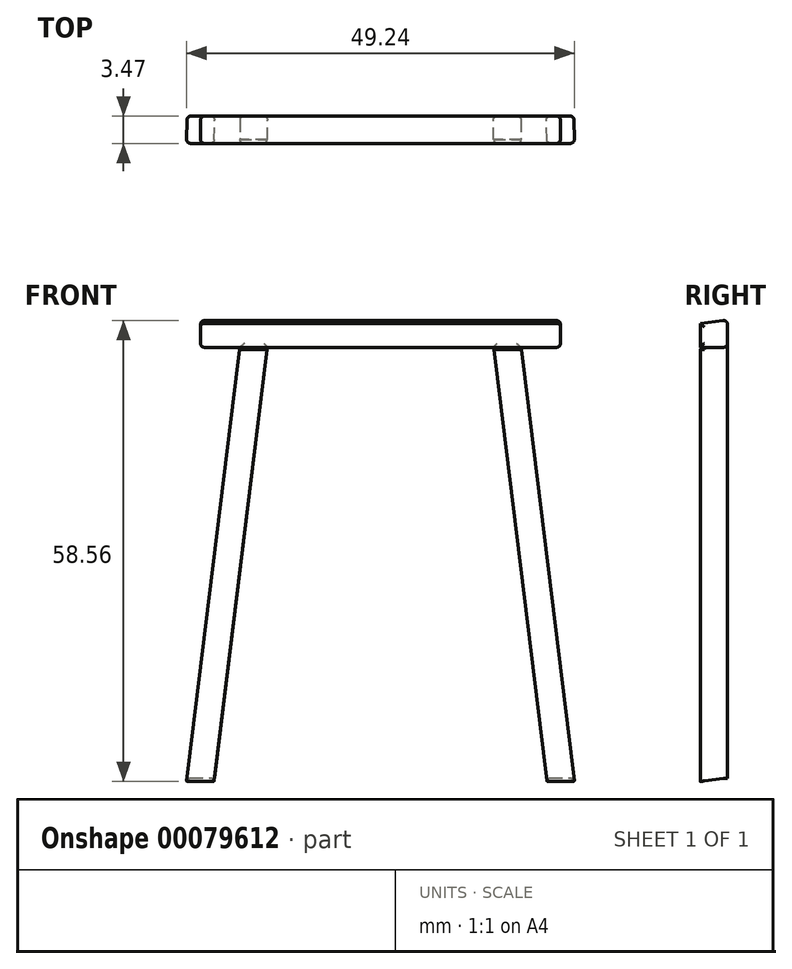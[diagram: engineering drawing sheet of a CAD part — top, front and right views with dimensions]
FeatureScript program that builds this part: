
annotation { "Feature Type Name" : "Feature", "Feature Type Description" : "" }
export const myFeature = defineFeature(function(context is Context, id is Id, definition is map)
    precondition{}
    {
        {
            var Q0;
            Q0=qCreatedBy(makeId("Front.planeOp"),FACE);
            var sketch = newSketch(context, id + "F0", { "sketchPlane" : qUnion([Q0])});
            skLineSegment(sketch, "E0.bottom", {"start": v(-22.86, -2.57) * mm, "end": v(22.86, -2.57) * mm});
            skLineSegment(sketch, "E0.top", {"start": v(-22.86, -6.05) * mm, "end": v(22.86, -6.05) * mm});
            skLineSegment(sketch, "E0.left", {"start": v(-22.86, -2.57) * mm, "end": v(-22.86, -6.05) * mm});
            skLineSegment(sketch, "E0.right", {"start": v(22.86, -2.57) * mm, "end": v(22.86, -6.05) * mm});
            skSolve(sketch);
        }
        {
            var Q0;
            Q0 = qSketchRegion(id + "F0", true);
            extrude(context, id + "F1", {"entities" : qUnion([Q0]), "depth" : 3.47 * mm});
        }
        {
            var Q0;
            Q0=makeQuery(id+"F1.opExtrude","CAP_FACE",FACE,{"disambiguationData":[OSD([sQuery(id+"F0.wireOp",EDGE,"E0.bottom"),sQuery(id+"F0.wireOp",EDGE,"E0.top"),sQuery(id+"F0.wireOp",EDGE,"E0.left"),sQuery(id+"F0.wireOp",EDGE,"E0.right")])],"isStart":false});
            var sketch = newSketch(context, id + "F2", { "sketchPlane" : qUnion([Q0])});
            skLineSegment(sketch, "E1", {"start": v(-17.43, -2.57) * mm, "end": v(-24.63, -61.2) * mm});
            skLineSegment(sketch, "E2", {"start": v(-24.63, -61.2) * mm, "end": v(-21.18, -61.63) * mm});
            skLineSegment(sketch, "E3", {"start": v(-21.18, -61.63) * mm, "end": v(-13.93, -2.57) * mm});
            skLineSegment(sketch, "E4", {"start": v(-13.93, -2.57) * mm, "end": v(-17.43, -2.57) * mm});
            skLineSegment(sketch, "E5.MirrorCS", {"start": v(24.63, -61.2) * mm, "end": v(21.18, -61.63) * mm});
            skLineSegment(sketch, "E6.MirrorCS", {"start": v(13.93, -2.57) * mm, "end": v(17.43, -2.57) * mm});
            skLineSegment(sketch, "E7.MirrorCS", {"start": v(17.43, -2.57) * mm, "end": v(24.63, -61.2) * mm});
            skLineSegment(sketch, "E8.MirrorCS", {"start": v(21.18, -61.63) * mm, "end": v(13.93, -2.57) * mm});
            skSolve(sketch);
        }
        {
            var Q0;
            Q0 = qSketchRegion(id + "F2", true);
            extrude(context, id + "F3", {"entities" : qUnion([Q0]), "operationType" : NewBodyOperationType.ADD, "oppositeDirection" : true, "depth" : 3.47 * mm});
        }
        {
            var Q0;
            Q0=qCreatedBy(makeId("Right.planeOp"),FACE);
            var sketch = newSketch(context, id + "F4", { "sketchPlane" : qUnion([Q0])});
            skLineSegment(sketch, "E9", {"start": v(0, -2.57) * mm, "end": v(-3.47, -2.57) * mm});
            skLineSegment(sketch, "E10", {"start": v(0, -2.57) * mm, "end": v(-3.47, -3) * mm});
            skLineSegment(sketch, "E11", {"start": v(-3.47, -2.57) * mm, "end": v(-3.47, -3) * mm});
            skPoint(sketch, "E12.orphan", {"position": v(-3.47, -3.03) * mm});
            skPoint(sketch, "E13.orphan", {"position": v(-3.7, -3.03) * mm});
            skLineSegment(sketch, "E14", {"start": v(-3.47, -61.2) * mm, "end": v(0, -60.78) * mm});
            skLineSegment(sketch, "E15", {"start": v(0, -60.78) * mm, "end": v(0, -61.96) * mm});
            skLineSegment(sketch, "E16", {"start": v(0, -61.96) * mm, "end": v(-3.47, -61.96) * mm});
            skLineSegment(sketch, "E17", {"start": v(-3.47, -61.96) * mm, "end": v(-3.47, -61.2) * mm});
            skSolve(sketch);
        }
        {
            var Q0;
            Q0 = qSketchRegion(id + "F4", true);
            extrude(context, id + "F5", {"entities" : qUnion([Q0]), "operationType" : NewBodyOperationType.REMOVE, "oppositeDirection" : true, "depth" : 76.2 * mm, "symmetric" : true});
        }
        {
            var Q0;
            Q0=makeQuery(id+"F3.boolean.opBoolean","MERGE",FACE,{"derivedFrom":[makeQuery(id+"F1.opExtrude","CAP_FACE",FACE,{"disambiguationData":[OSD([sQuery(id+"F0.wireOp",EDGE,"E0.bottom"),sQuery(id+"F0.wireOp",EDGE,"E0.top"),sQuery(id+"F0.wireOp",EDGE,"E0.left"),sQuery(id+"F0.wireOp",EDGE,"E0.right")])],"isStart":false}),makeQuery(id+"F3.opExtrude","CAP_FACE",FACE,{"disambiguationData":[OSD([sQuery(id+"F2.wireOp",EDGE,"E1"),sQuery(id+"F2.wireOp",EDGE,"E2"),sQuery(id+"F2.wireOp",EDGE,"E3"),sQuery(id+"F2.wireOp",EDGE,"E4")])],"isStart":true}),makeQuery(id+"F3.opExtrude","CAP_FACE",FACE,{"disambiguationData":[OSD([sQuery(id+"F2.wireOp",EDGE,"E5.MirrorCS"),sQuery(id+"F2.wireOp",EDGE,"E6.MirrorCS"),sQuery(id+"F2.wireOp",EDGE,"E7.MirrorCS"),sQuery(id+"F2.wireOp",EDGE,"E8.MirrorCS")])],"isStart":true})]});
            var sketch = newSketch(context, id + "F6", { "sketchPlane" : qUnion([Q0])});
            skLineSegment(sketch, "E18", {"start": v(-22.86, -6.05) * mm, "end": v(22.86, -6.05) * mm});
            skLineSegment(sketch, "E19", {"start": v(22.86, -6.05) * mm, "end": v(22.86, -6.3) * mm});
            skLineSegment(sketch, "E20", {"start": v(22.86, -6.3) * mm, "end": v(-22.86, -6.3) * mm});
            skLineSegment(sketch, "E21", {"start": v(-22.86, -6.3) * mm, "end": v(-22.86, -6.05) * mm});
            skSolve(sketch);
        }
        {
            var Q0;
            Q0 = qSketchRegion(id + "F6", true);
            extrude(context, id + "F7", {"entities" : qUnion([Q0]), "operationType" : NewBodyOperationType.REMOVE, "oppositeDirection" : true, "depth" : 0.5 * mm});
        }
        {
            var Q0;
            Q0=makeQuery(id+"F5.boolean.opBoolean","COPY",EDGE,{"derivedFrom":makeQuery(id+"F5.opExtrude","SWEPT_EDGE",EDGE,{"disambiguationData":[OSD([sQuery(id+"F4.wireOp",EDGE,"E10"),sQuery(id+"F4.wireOp",EDGE,"E11")])]})});
            var Q1;
            Q1=makeQuery(id+"F1.opExtrude","SWEPT_FACE",FACE,{"disambiguationData":[OSD([sQuery(id+"F0.wireOp",EDGE,"E0.right")])]});
            var Q2;
            Q2=makeQuery(id+"F3.opExtrude","CAP_EDGE",EDGE,{"disambiguationData":[OSD([sQuery(id+"F2.wireOp",EDGE,"E7.MirrorCS")])],"isStart":true});
            var Q3;
            Q3=makeQuery(id+"F3.opExtrude","CAP_EDGE",EDGE,{"disambiguationData":[OSD([sQuery(id+"F2.wireOp",EDGE,"E3")])],"isStart":true});
            var Q4;
            Q4=makeQuery(id+"F3.opExtrude","CAP_EDGE",EDGE,{"disambiguationData":[OSD([sQuery(id+"F2.wireOp",EDGE,"E1")])],"isStart":true});
            var Q5;
            Q5=makeQuery(id+"F1.opExtrude","SWEPT_FACE",FACE,{"disambiguationData":[OSD([sQuery(id+"F0.wireOp",EDGE,"E0.left")])]});
            var Q6;
            Q6=makeQuery(id+"F3.opExtrude","CAP_EDGE",EDGE,{"disambiguationData":[OSD([sQuery(id+"F2.wireOp",EDGE,"E8.MirrorCS")])],"isStart":true});
            var Q7;
            {var subQ0=sQuery(id+"F0.wireOp",EDGE,"E0.right");var subQ1=sQuery(id+"F0.wireOp",EDGE,"E0.top");Q7=makeQuery(id+"F3.boolean.opBoolean","SPLIT",EDGE,{"disambiguationData":[TD([makeQuery(id+"F1.opExtrude","SWEPT_FACE",FACE,{"disambiguationData":[OSD([subQ0])]})])],"derivedFrom":makeQuery(id+"F1.opExtrude","CAP_EDGE",EDGE,{"disambiguationData":[OSD([subQ1])],"isStart":true})});}
            var Q8;
            Q8=makeQuery(id+"F3.opExtrude","CAP_EDGE",EDGE,{"disambiguationData":[OSD([sQuery(id+"F2.wireOp",EDGE,"E8.MirrorCS")])],"isStart":false});
            var Q9;
            {var subQ0=sQuery(id+"F2.wireOp",EDGE,"E3");var subQ1=sQuery(id+"F0.wireOp",EDGE,"E0.top");Q9=makeQuery(id+"F3.boolean.opBoolean","SPLIT",EDGE,{"disambiguationData":[TD([makeQuery(id+"F3.opExtrude","SWEPT_FACE",FACE,{"disambiguationData":[OSD([subQ0])]})])],"derivedFrom":makeQuery(id+"F1.opExtrude","CAP_EDGE",EDGE,{"disambiguationData":[OSD([subQ1])],"isStart":true})});}
            var Q10;
            {var subQ0=sQuery(id+"F0.wireOp",EDGE,"E0.left");var subQ1=sQuery(id+"F0.wireOp",EDGE,"E0.top");Q10=makeQuery(id+"F3.boolean.opBoolean","SPLIT",EDGE,{"disambiguationData":[TD([makeQuery(id+"F1.opExtrude","SWEPT_FACE",FACE,{"disambiguationData":[OSD([subQ0])]})])],"derivedFrom":makeQuery(id+"F1.opExtrude","CAP_EDGE",EDGE,{"disambiguationData":[OSD([subQ1])],"isStart":true})});}
            var Q11;
            Q11=makeQuery(id+"F3.opExtrude","CAP_EDGE",EDGE,{"disambiguationData":[OSD([sQuery(id+"F2.wireOp",EDGE,"E1")])],"isStart":false});
            var Q12;
            Q12=makeQuery(id+"F3.opExtrude","CAP_EDGE",EDGE,{"disambiguationData":[OSD([sQuery(id+"F2.wireOp",EDGE,"E3")])],"isStart":false});
            var Q13;
            Q13=makeQuery(id+"F3.opExtrude","CAP_EDGE",EDGE,{"disambiguationData":[OSD([sQuery(id+"F2.wireOp",EDGE,"E7.MirrorCS")])],"isStart":false});
            var Q14;
            {var subQ0=sQuery(id+"F2.wireOp",EDGE,"E3");var subQ3=sQuery(id+"F0.wireOp",EDGE,"E0.top");var subQ5=sQuery(id+"F0.wireOp",EDGE,"E0.right");var subQ6=sQuery(id+"F0.wireOp",EDGE,"E0.left");var subQ11=makeQuery(id+"F1.opExtrude","CAP_EDGE",EDGE,{"disambiguationData":[OSD([subQ3])],"isStart":false});Q14=makeQuery(id+"F7.boolean.opBoolean","MERGE",EDGE,{"derivedFrom":[makeQuery(id+"F3.boolean.opBoolean","SPLIT",EDGE,{"disambiguationData":[TD([makeQuery(id+"F1.opExtrude","SWEPT_FACE",FACE,{"disambiguationData":[OSD([subQ6])]})])],"derivedFrom":subQ11}),makeQuery(id+"F3.boolean.opBoolean","SPLIT",EDGE,{"disambiguationData":[TD([makeQuery(id+"F1.opExtrude","SWEPT_FACE",FACE,{"disambiguationData":[OSD([subQ5])]})])],"derivedFrom":subQ11}),makeQuery(id+"F3.boolean.opBoolean","SPLIT",EDGE,{"disambiguationData":[TD([makeQuery(id+"F3.opExtrude","SWEPT_FACE",FACE,{"disambiguationData":[OSD([subQ0])]})])],"derivedFrom":subQ11}),makeQuery(id+"F7.opExtrude","CAP_EDGE",EDGE,{"disambiguationData":[OSD([sQuery(id+"F6.wireOp",EDGE,"E18")])],"isStart":true})]});}
            var Q15;
            Q15=makeQuery(id+"F5.boolean.opBoolean","MERGE",EDGE,{"derivedFrom":[makeQuery(id+"F1.opExtrude","CAP_EDGE",EDGE,{"disambiguationData":[OSD([sQuery(id+"F0.wireOp",EDGE,"E0.bottom")])],"isStart":true}),makeQuery(id+"F5.opExtrude","SWEPT_EDGE",EDGE,{"disambiguationData":[OSD([sQuery(id+"F4.wireOp",EDGE,"E9"),sQuery(id+"F4.wireOp",EDGE,"E10")])]})]});
            fillet(context, id + "F8", {"entities" : qUnion([Q0, Q1, Q2, Q3, Q4, Q5, Q6, Q7, Q8, Q9, Q10, Q11, Q12, Q13, Q14, Q15]), "radius" : 0.5 * mm, "tangentPropagation" : true, "allowEdgeOverflow" : false});
        }
    });
